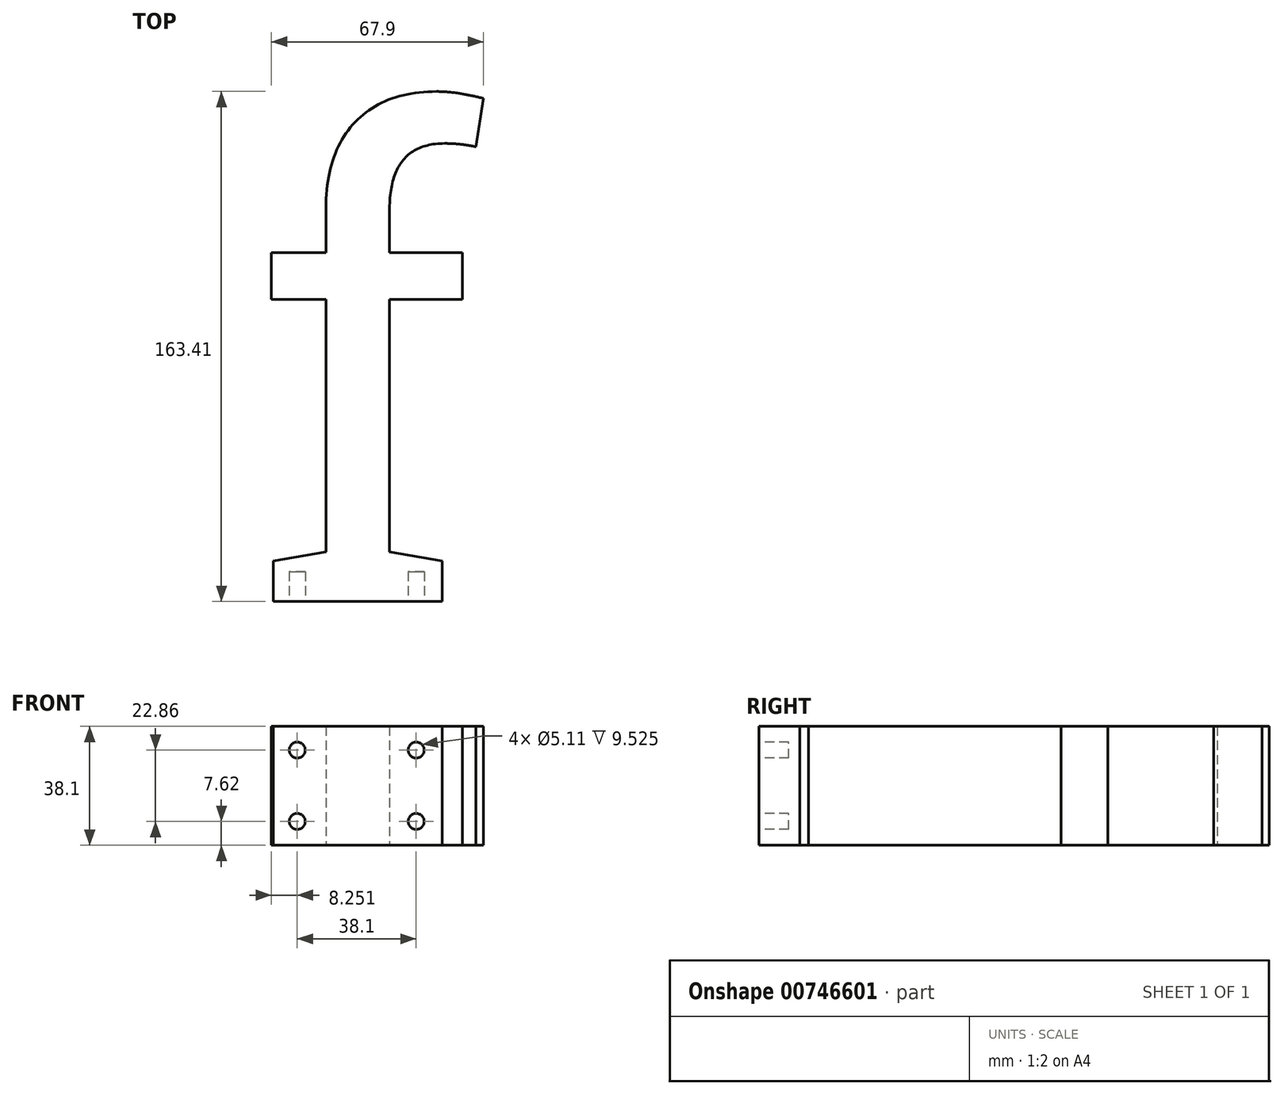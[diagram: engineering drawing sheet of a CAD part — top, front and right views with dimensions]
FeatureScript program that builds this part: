
annotation { "Feature Type Name" : "Feature", "Feature Type Description" : "" }
export const myFeature = defineFeature(function(context is Context, id is Id, definition is map)
    precondition{}
    {
        {
            var Q0;
            Q0=qCreatedBy(makeId("Top.planeOp"),FACE);
            var sketch = newSketch(context, id + "F0", { "sketchPlane" : qUnion([Q0])});
            skText(sketch, "E0", { "text": "f", "fontName": "RobotoSlab-Regular.ttf"});
            const initialGuessF0  = {"E0": [0, 0, 1, 0, 0.1524]};
            skSetInitialGuess(sketch, initialGuessF0);
            skSolve(sketch);
        }
        {
            var Q0;
            Q0=makeQuery(id+"F0.imprint","IMPRINT",FACE,{"disambiguationData":[TD([[makeQuery(id+"F0.imprint","IMPRINT",EDGE,{"derivedFrom":sQuery(id+"F0.wireOp",EDGE,"E0.sketch_text.stroke-0")}),-1.0]])]});
            extrude(context, id + "F1", {"entities" : qUnion([Q0]), "depth" : 38.1 * mm, "offsetDistance" : 25.4 * mm});
        }
        {
            var Q0;
            Q0=makeQuery(id+"F1.opExtrude","SWEPT_FACE",FACE,{"disambiguationData":[OSD([sQuery(id+"F0.wireOp",EDGE,"E0.sketch_text.stroke-19")])]});
            var sketch = newSketch(context, id + "F2", { "sketchPlane" : qUnion([Q0])});
            skCircle(sketch, "E1", {"center": v(15.5, 30.48) * mm, "radius": 2.55 * mm});
            skCircle(sketch, "E2", {"center": v(15.5, 7.62) * mm, "radius": 2.55 * mm});
            skCircle(sketch, "E3", {"center": v(53.6, 30.48) * mm, "radius": 2.55 * mm});
            skCircle(sketch, "E4", {"center": v(53.6, 7.62) * mm, "radius": 2.55 * mm});
            skSolve(sketch);
        }
        {
            var Q0;
            Q0 = qSketchRegion(id + "F2", true);
            extrude(context, id + "F3", {"entities" : qUnion([Q0]), "operationType" : NewBodyOperationType.REMOVE, "oppositeDirection" : true, "depth" : 9.52 * mm, "offsetDistance" : 25.4 * mm});
        }
    });
